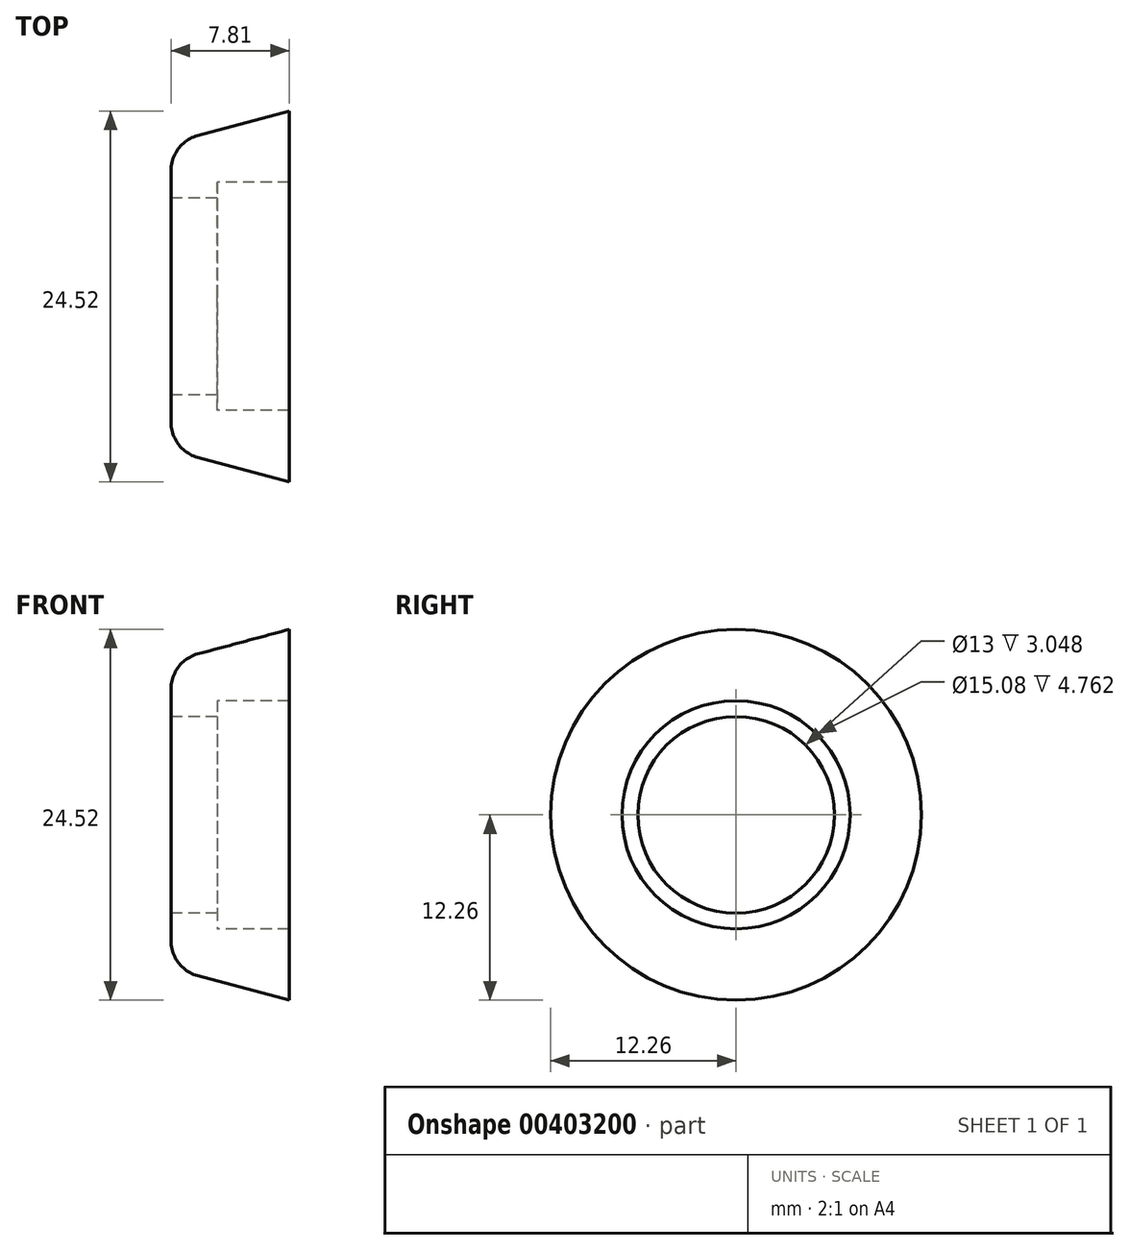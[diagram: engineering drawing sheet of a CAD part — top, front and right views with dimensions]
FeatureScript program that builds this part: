
annotation { "Feature Type Name" : "Feature", "Feature Type Description" : "" }
export const myFeature = defineFeature(function(context is Context, id is Id, definition is map)
    precondition{}
    {
        {
            var Q0;
            Q0=qCreatedBy(makeId("Front.planeOp"),FACE);
            var sketch = newSketch(context, id + "F0", { "sketchPlane" : qUnion([Q0])});
            skLineSegment(sketch, "E0", {"start": v(0, 12.26) * mm, "end": v(-6.05, 10.64) * mm});
            skLineSegment(sketch, "E1", {"start": v(-7.81, 8.34) * mm, "end": v(-7.81, 6.5) * mm});
            skPoint(sketch, "E2.visualSharp", {"position": v(-7.81, 10.16) * mm});
            skArc(sketch, "E2.filletArc", {"start": v(-6.05, 10.64) * mm, "mid": v(-7.32, 9.79) * mm, "end": v(-7.81, 8.34) * mm});
            skLineSegment(sketch, "E3", {"start": v(0, 12.26) * mm, "end": v(0, 7.54) * mm});
            skLineSegment(sketch, "E4", {"start": v(-79.3, 0) * mm, "end": v(89.8, 0) * mm, "construction": true});
            skLineSegment(sketch, "E5", {"start": v(-7.81, 6.5) * mm, "end": v(-4.76, 6.5) * mm});
            skLineSegment(sketch, "E6", {"start": v(-4.76, 6.5) * mm, "end": v(-4.76, 7.54) * mm});
            skLineSegment(sketch, "E7", {"start": v(-4.76, 7.54) * mm, "end": v(0, 7.54) * mm});
            skSolve(sketch);
        }
        {
            var Q0;
            Q0=makeQuery(id+"F0.imprint","IMPRINT",FACE,{"disambiguationData":[TD([[makeQuery(id+"F0.imprint","IMPRINT",EDGE,{"derivedFrom":sQuery(id+"F0.wireOp",EDGE,"iFIy6t9p-DLf4-Kr0U-XxBy-TVTDalWC6sph")}),1.0]])]});
            var Q1;
            Q1=makeQuery(id+"F0.imprint","IMPRINT",FACE,{"disambiguationData":[TD([[makeQuery(id+"F0.imprint","IMPRINT",EDGE,{"derivedFrom":sQuery(id+"F0.wireOp",EDGE,"E0")}),1.0]])]});
            var Q2;
            Q2=sQuery(id+"F0.wireOp",EDGE,"E4");
            revolve(context, id + "F1", {"entities" : qUnion([Q0, Q1]), "axis" : qUnion([Q2]), "revolveType" : RevolveType.FULL});
        }
    });
